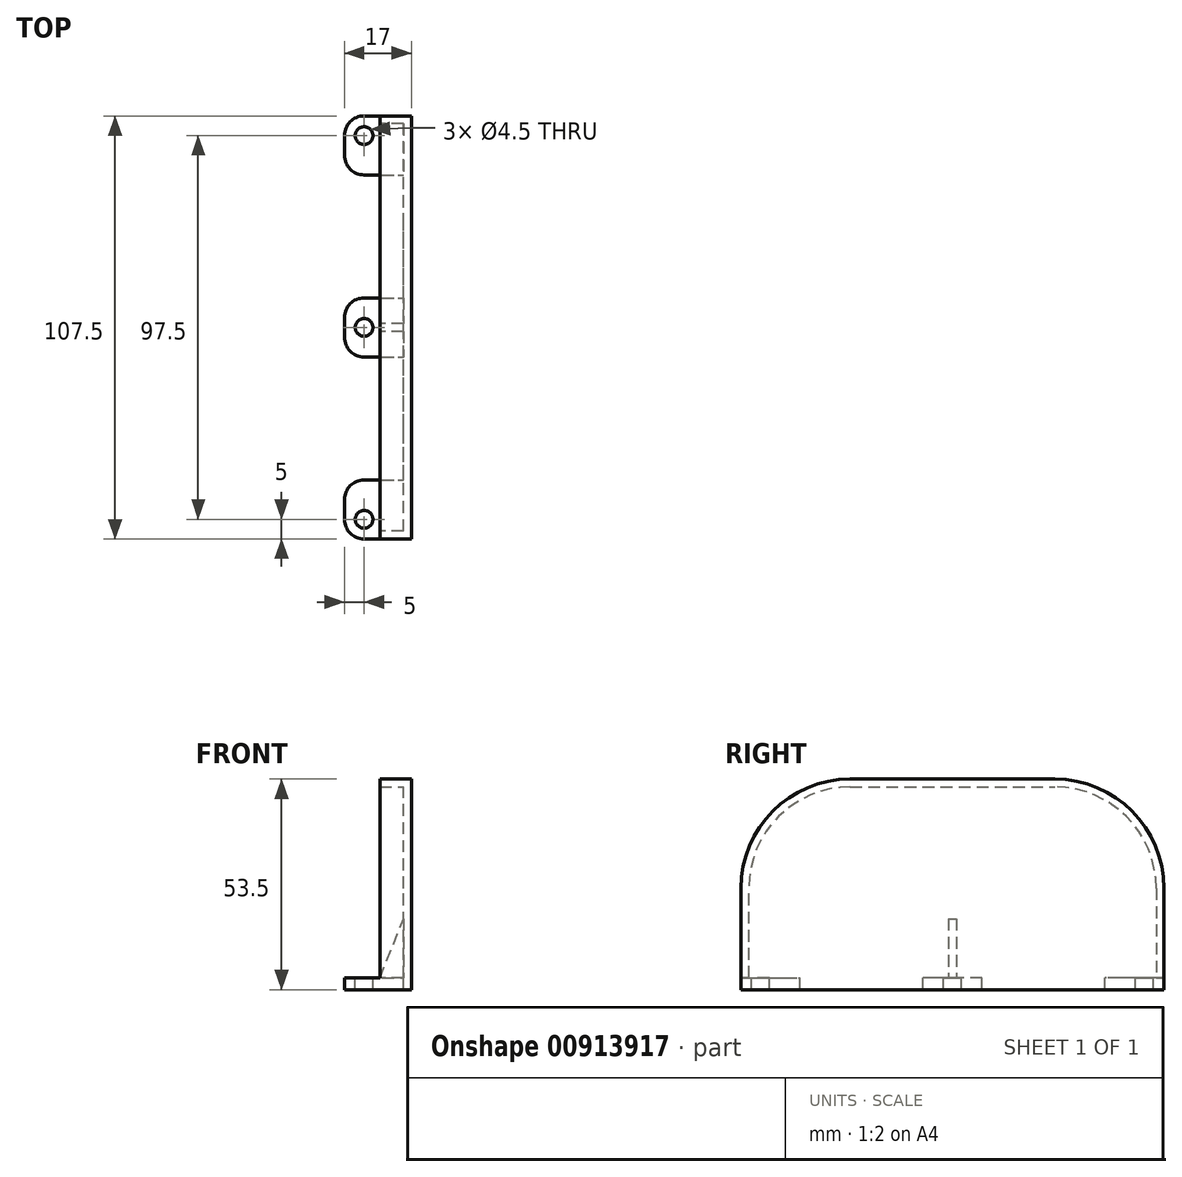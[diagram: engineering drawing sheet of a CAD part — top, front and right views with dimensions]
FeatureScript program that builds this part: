
annotation { "Feature Type Name" : "Feature", "Feature Type Description" : "" }
export const myFeature = defineFeature(function(context is Context, id is Id, definition is map)
    precondition{}
    {
        {
            var Q0;
            Q0=qCreatedBy(makeId("Right.planeOp"),FACE);
            var sketch = newSketch(context, id + "F0", { "sketchPlane" : qUnion([Q0])});
            skLineSegment(sketch, "E0.bottom", {"start": v(-53.75, 0) * mm, "end": v(53.75, 0) * mm});
            skLineSegment(sketch, "E0.top", {"start": v(-26, 53.5) * mm, "end": v(26, 53.5) * mm});
            skLineSegment(sketch, "E0.left", {"start": v(-53.75, 0) * mm, "end": v(-53.75, 25.75) * mm});
            skLineSegment(sketch, "E0.right", {"start": v(53.75, 0) * mm, "end": v(53.75, 25.75) * mm});
            skPoint(sketch, "E1.visualSharp", {"position": v(-53.75, 53.5) * mm});
            skArc(sketch, "E1.filletArc", {"start": v(-26, 53.5) * mm, "mid": v(-45.62, 45.37) * mm, "end": v(-53.75, 25.75) * mm});
            skPoint(sketch, "E2.visualSharp", {"position": v(53.75, 53.5) * mm});
            skArc(sketch, "E2.filletArc", {"start": v(53.75, 25.75) * mm, "mid": v(45.62, 45.37) * mm, "end": v(26, 53.5) * mm});
            skLineSegment(sketch, "E3", {"start": v(-53.75, 25.75) * mm, "end": v(53.75, 25.75) * mm, "construction": true});
            skSolve(sketch);
        }
        {
            var Q0;
            Q0=qSketchRegion(id+"F0",true);
            extrude(context, id + "F1", {"entities" : qUnion([Q0]), "depth" : 2 * mm, "offsetDistance" : 25 * mm});
        }
        {
            var Q0;
            Q0=makeQuery(id+"F1.opExtrude","CAP_FACE",FACE,{"disambiguationData":[OSD([sQuery(id+"F0.wireOp",EDGE,"E0.bottom"),sQuery(id+"F0.wireOp",EDGE,"E0.top"),sQuery(id+"F0.wireOp",EDGE,"E0.left"),sQuery(id+"F0.wireOp",EDGE,"E0.right"),sQuery(id+"F0.wireOp",EDGE,"E1.filletArc"),sQuery(id+"F0.wireOp",EDGE,"E2.filletArc"),sQuery(id+"F0.wireOp",EDGE,"wrzfFsvl-UCqs-aezh-ijM7-L5YhXrz3E0mf"),sQuery(id+"F0.wireOp",EDGE,"b7c118de-4fc0-4959-914e-51f86bd052230.MirrorC"),sQuery(id+"F0.wireOp",EDGE,"14c775e2-4603-4bff-89f2-d9301d5ced190.MirrorC"),sQuery(id+"F0.wireOp",EDGE,"2ef91e9a-52c1-4320-9fba-dc354453fdb00.MirrorC")])],"isStart":true});
            var sketch = newSketch(context, id + "F2", { "sketchPlane" : qUnion([Q0])});
            skArc(sketch, "E4.0", {"start": v(51.75, 25.75) * mm, "mid": v(44.2, 43.96) * mm, "end": v(26, 51.5) * mm});
            skArc(sketch, "E4.1", {"start": v(-26, 51.5) * mm, "mid": v(-44.2, 43.96) * mm, "end": v(-51.75, 25.75) * mm});
            skLineSegment(sketch, "E4.2", {"start": v(-51.75, 25.75) * mm, "end": v(-51.75, 0) * mm});
            skLineSegment(sketch, "E4.3", {"start": v(26, 51.5) * mm, "end": v(-26, 51.5) * mm});
            skLineSegment(sketch, "E4.5", {"start": v(51.75, 0) * mm, "end": v(51.75, 25.75) * mm});
            skArc(sketch, "E5.0", {"start": v(53.75, 25.75) * mm, "mid": v(45.62, 45.37) * mm, "end": v(26, 53.5) * mm});
            skArc(sketch, "E5.1", {"start": v(-26, 53.5) * mm, "mid": v(-45.62, 45.37) * mm, "end": v(-53.75, 25.75) * mm});
            skLineSegment(sketch, "E5.2", {"start": v(-53.75, 25.75) * mm, "end": v(-53.75, 0) * mm});
            skLineSegment(sketch, "E5.3", {"start": v(26, 53.5) * mm, "end": v(-26, 53.5) * mm});
            skLineSegment(sketch, "E5.4", {"start": v(-53.75, 0) * mm, "end": v(-51.75, 0) * mm});
            skLineSegment(sketch, "E5.5", {"start": v(53.75, 0) * mm, "end": v(53.75, 25.75) * mm});
            skLineSegment(sketch, "E6.trimOffspring", {"start": v(51.75, 0) * mm, "end": v(53.75, 0) * mm});
            skSolve(sketch);
        }
        {
            var Q0;
            Q0=qSketchRegion(id+"F2",true);
            extrude(context, id + "F3", {"entities" : qUnion([Q0]), "operationType" : NewBodyOperationType.ADD, "depth" : 6 * mm, "offsetDistance" : 25 * mm});
        }
        {
            var Q0;
            Q0=makeQuery(id+"F1.opExtrude","CAP_FACE",FACE,{"disambiguationData":[OSD([sQuery(id+"F0.wireOp",EDGE,"E0.bottom"),sQuery(id+"F0.wireOp",EDGE,"E0.top"),sQuery(id+"F0.wireOp",EDGE,"E0.left"),sQuery(id+"F0.wireOp",EDGE,"E0.right"),sQuery(id+"F0.wireOp",EDGE,"E1.filletArc"),sQuery(id+"F0.wireOp",EDGE,"E2.filletArc")])],"isStart":true});
            var sketch = newSketch(context, id + "F4", { "sketchPlane" : qUnion([Q0])});
            skLineSegment(sketch, "E7.bottom", {"start": v(-7.5, 0) * mm, "end": v(7.5, 0) * mm});
            skLineSegment(sketch, "E7.top", {"start": v(-7.5, 3) * mm, "end": v(7.5, 3) * mm});
            skLineSegment(sketch, "E7.left", {"start": v(-7.5, 0) * mm, "end": v(-7.5, 3) * mm});
            skLineSegment(sketch, "E7.right", {"start": v(7.5, 0) * mm, "end": v(7.5, 3) * mm});
            skLineSegment(sketch, "E8.bottom", {"start": v(-53.75, 0) * mm, "end": v(-38.75, 0) * mm});
            skLineSegment(sketch, "E8.top", {"start": v(-53.75, 3) * mm, "end": v(-38.75, 3) * mm});
            skLineSegment(sketch, "E8.left", {"start": v(-53.75, 0) * mm, "end": v(-53.75, 3) * mm});
            skLineSegment(sketch, "E8.right", {"start": v(-38.75, 0) * mm, "end": v(-38.75, 3) * mm});
            skLineSegment(sketch, "E9.MirrorCS", {"start": v(53.75, 0) * mm, "end": v(53.75, 3) * mm});
            skLineSegment(sketch, "E10.MirrorCS", {"start": v(53.75, 3) * mm, "end": v(38.75, 3) * mm});
            skLineSegment(sketch, "E11.MirrorCS", {"start": v(38.75, 0) * mm, "end": v(38.75, 3) * mm});
            skLineSegment(sketch, "E12.MirrorCS", {"start": v(53.75, 0) * mm, "end": v(38.75, 0) * mm});
            skSolve(sketch);
        }
        {
            var Q0;
            Q0=qSketchRegion(id+"F4",true);
            extrude(context, id + "F5", {"entities" : qUnion([Q0]), "operationType" : NewBodyOperationType.ADD, "depth" : 15 * mm, "offsetDistance" : 25 * mm});
        }
        {
            var Q0;
            Q0=qCreatedBy(makeId("Front.planeOp"),FACE);
            var sketch = newSketch(context, id + "F6", { "sketchPlane" : qUnion([Q0])});
            skLineSegment(sketch, "E13", {"start": v(-6, 3) * mm, "end": v(0, 18) * mm});
            skLineSegment(sketch, "E14", {"start": v(0, 18) * mm, "end": v(0, 3) * mm});
            skLineSegment(sketch, "E15", {"start": v(0, 3) * mm, "end": v(-6, 3) * mm});
            skSolve(sketch);
        }
        {
            var Q0;
            Q0=qSketchRegion(id+"F6",true);
            extrude(context, id + "F7", {"entities" : qUnion([Q0]), "operationType" : NewBodyOperationType.ADD, "endBound" : BoundingType.SYMMETRIC, "depth" : 2 * mm, "offsetDistance" : 25 * mm});
        }
        {
            var Q0;
            Q0=makeQuery(id+"F5.opExtrude","SWEPT_FACE",FACE,{"disambiguationData":[OSD([sQuery(id+"F4.wireOp",EDGE,"E8.top")])]});
            var sketch = newSketch(context, id + "F8", { "sketchPlane" : qUnion([Q0])});
            skCircle(sketch, "E16", {"center": v(-10, 48.75) * mm, "radius": 2.25 * mm});
            skCircle(sketch, "E17", {"center": v(-10, 0) * mm, "radius": 2.25 * mm});
            skCircle(sketch, "E18", {"center": v(-10, -48.75) * mm, "radius": 2.25 * mm});
            skSolve(sketch);
        }
        {
            var Q0;
            Q0=qSketchRegion(id+"F8",true);
            extrude(context, id + "F9", {"entities" : qUnion([Q0]), "operationType" : NewBodyOperationType.REMOVE, "endBound" : BoundingType.THROUGH_ALL, "oppositeDirection" : true, "depth" : 25 * mm, "offsetDistance" : 25 * mm});
        }
        {
            var Q0;
            Q0=makeQuery(id+"F5.opExtrude","CAP_EDGE",EDGE,{"disambiguationData":[OSD([sQuery(id+"F4.wireOp",EDGE,"E9.MirrorCS")])],"isStart":false});
            var Q1;
            Q1=makeQuery(id+"F5.opExtrude","CAP_EDGE",EDGE,{"disambiguationData":[OSD([sQuery(id+"F4.wireOp",EDGE,"E8.left")])],"isStart":false});
            var Q2;
            Q2=makeQuery(id+"F5.opExtrude","CAP_EDGE",EDGE,{"disambiguationData":[OSD([sQuery(id+"F4.wireOp",EDGE,"E8.right")])],"isStart":false});
            var Q3;
            Q3=makeQuery(id+"F5.opExtrude","CAP_EDGE",EDGE,{"disambiguationData":[OSD([sQuery(id+"F4.wireOp",EDGE,"E7.left")])],"isStart":false});
            var Q4;
            Q4=makeQuery(id+"F5.opExtrude","CAP_EDGE",EDGE,{"disambiguationData":[OSD([sQuery(id+"F4.wireOp",EDGE,"E7.right")])],"isStart":false});
            var Q5;
            Q5=makeQuery(id+"F5.opExtrude","CAP_EDGE",EDGE,{"disambiguationData":[OSD([sQuery(id+"F4.wireOp",EDGE,"E11.MirrorCS")])],"isStart":false});
            fillet(context, id + "F10", {"entities" : qUnion([Q0, Q1, Q2, Q3, Q4, Q5]), "radius" : 5 * mm, "tangentPropagation" : true, "allowEdgeOverflow" : false});
        }
    });
